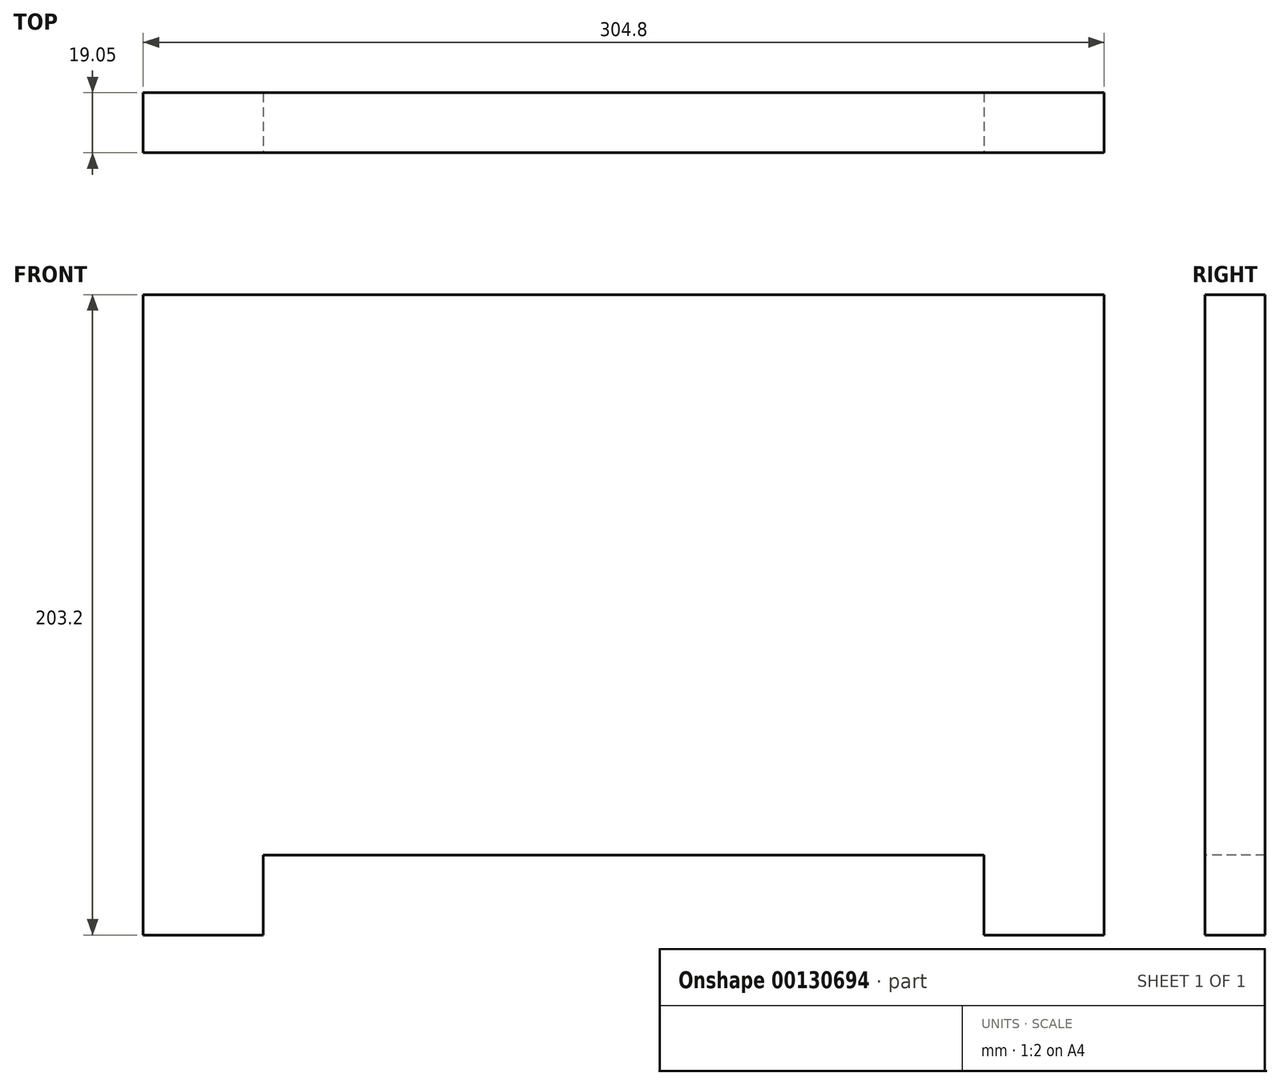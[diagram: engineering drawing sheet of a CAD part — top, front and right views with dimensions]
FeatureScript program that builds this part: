
annotation { "Feature Type Name" : "Feature", "Feature Type Description" : "" }
export const myFeature = defineFeature(function(context is Context, id is Id, definition is map)
    precondition{}
    {
        {
            var Q0;
            Q0=qCreatedBy(makeId("Front.planeOp"),FACE);
            var sketch = newSketch(context, id + "F0", { "sketchPlane" : qUnion([Q0])});
            skLineSegment(sketch, "E0.bottom", {"start": v(0, 0) * mm, "end": v(304.8, 0) * mm});
            skLineSegment(sketch, "E0.top", {"start": v(0, 203.2) * mm, "end": v(304.8, 203.2) * mm});
            skLineSegment(sketch, "E0.left", {"start": v(0, 0) * mm, "end": v(0, 203.2) * mm});
            skLineSegment(sketch, "E0.right", {"start": v(304.8, 0) * mm, "end": v(304.8, 203.2) * mm});
            skSolve(sketch);
        }
        {
            var Q0;
            Q0 = qSketchRegion(id + "F0", true);
            extrude(context, id + "F1", {"entities" : qUnion([Q0]), "depth" : 19.05 * mm});
        }
        {
            var Q0;
            Q0=makeQuery(id+"F1.opExtrude","CAP_FACE",FACE,{"disambiguationData":[OSD([sQuery(id+"F0.wireOp",EDGE,"E0.bottom"),sQuery(id+"F0.wireOp",EDGE,"E0.top"),sQuery(id+"F0.wireOp",EDGE,"E0.left"),sQuery(id+"F0.wireOp",EDGE,"E0.right")])],"isStart":false});
            var sketch = newSketch(context, id + "F2", { "sketchPlane" : qUnion([Q0])});
            skLineSegment(sketch, "E1.bottom", {"start": v(38.1, 25.4) * mm, "end": v(266.7, 25.4) * mm});
            skLineSegment(sketch, "E1.top", {"start": v(38.1, 0) * mm, "end": v(266.7, 0) * mm});
            skLineSegment(sketch, "E1.left", {"start": v(38.1, 25.4) * mm, "end": v(38.1, 0) * mm});
            skLineSegment(sketch, "E1.right", {"start": v(266.7, 25.4) * mm, "end": v(266.7, 0) * mm});
            skSolve(sketch);
        }
        {
            var Q0;
            Q0=makeQuery(id+"F2.imprint","IMPRINT",FACE,{"disambiguationData":[TD([[makeQuery(id+"F2.imprint","IMPRINT",EDGE,{"derivedFrom":sQuery(id+"F2.wireOp",EDGE,"E1.bottom")}),-1.0]])]});
            extrude(context, id + "F3", {"entities" : qUnion([Q0]), "operationType" : NewBodyOperationType.REMOVE, "endBound" : BoundingType.THROUGH_ALL, "oppositeDirection" : true, "depth" : 25.4 * mm});
        }
    });
